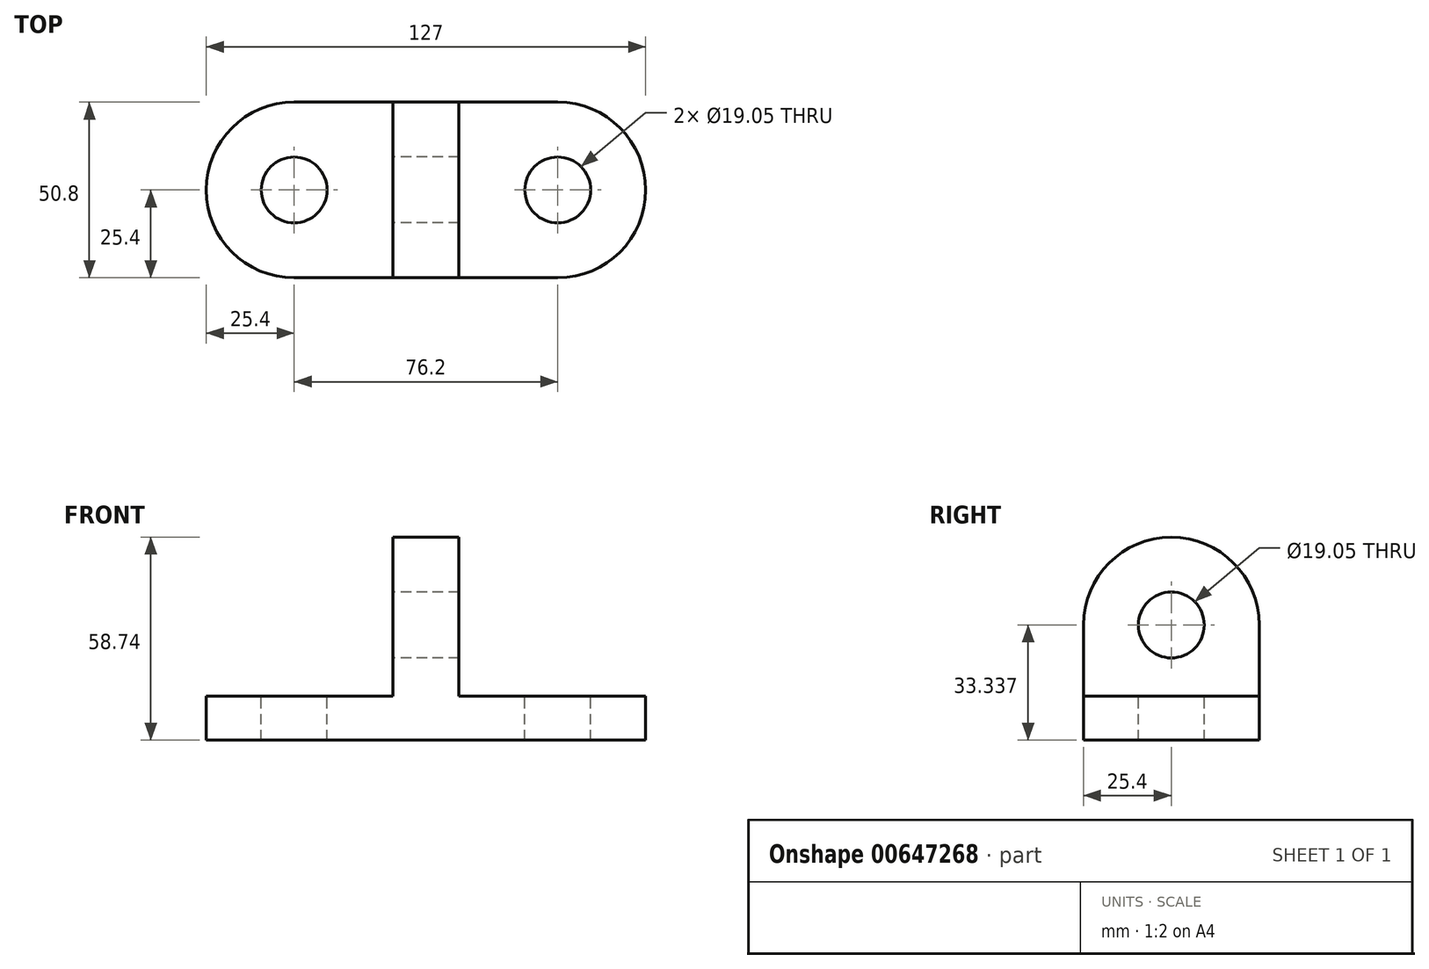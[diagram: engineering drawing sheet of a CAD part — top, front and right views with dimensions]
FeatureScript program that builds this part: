
annotation { "Feature Type Name" : "Feature", "Feature Type Description" : "" }
export const myFeature = defineFeature(function(context is Context, id is Id, definition is map)
    precondition{}
    {
        {
            var Q0;
            Q0=qCreatedBy(makeId("Top.planeOp"),FACE);
            var sketch = newSketch(context, id + "F0", { "sketchPlane" : qUnion([Q0])});
            skLineSegment(sketch, "E0.bottom", {"start": v(-38.1, -25.4) * mm, "end": v(38.1, -25.4) * mm});
            skLineSegment(sketch, "E0.top", {"start": v(-38.1, 25.4) * mm, "end": v(38.1, 25.4) * mm});
            skPoint(sketch, "E0.middle", {"position": v(0, 0) * mm});
            skArc(sketch, "E1", {"start": v(-38.1, -25.4) * mm, "mid": v(-63.5, 0) * mm, "end": v(-38.1, 25.4) * mm});
            skArc(sketch, "E2", {"start": v(38.1, -25.4) * mm, "mid": v(63.5, 0) * mm, "end": v(38.1, 25.4) * mm});
            skSolve(sketch);
        }
        {
            var Q0;
            Q0 = qSketchRegion(id + "F0", true);
            extrude(context, id + "F1", {"entities" : qUnion([Q0]), "depth" : 12.7 * mm, "offsetDistance" : 25.4 * mm});
        }
        {
            var Q0;
            Q0=makeQuery(id+"F1.opExtrude","CAP_FACE",FACE,{"disambiguationData":[OSD([sQuery(id+"F0.wireOp",EDGE,"E0.bottom"),sQuery(id+"F0.wireOp",EDGE,"E0.top"),sQuery(id+"F0.wireOp",EDGE,"E1"),sQuery(id+"F0.wireOp",EDGE,"E2")])],"isStart":false});
            var sketch = newSketch(context, id + "F2", { "sketchPlane" : qUnion([Q0])});
            skCircle(sketch, "E3", {"center": v(-38.1, 0) * mm, "radius": 9.53 * mm});
            skCircle(sketch, "E4", {"center": v(38.1, 0) * mm, "radius": 9.53 * mm});
            skSolve(sketch);
        }
        {
            var Q0;
            Q0=makeQuery(id+"F2.imprint","IMPRINT",FACE,{"disambiguationData":[TD([[makeQuery(id+"F2.imprint","IMPRINT",EDGE,{"derivedFrom":sQuery(id+"F2.wireOp",EDGE,"E3")}),1.0]])]});
            var Q1;
            Q1=makeQuery(id+"F2.imprint","IMPRINT",FACE,{"disambiguationData":[TD([[makeQuery(id+"F2.imprint","IMPRINT",EDGE,{"derivedFrom":sQuery(id+"F2.wireOp",EDGE,"E4")}),1.0]])]});
            extrude(context, id + "F3", {"entities" : qUnion([Q0, Q1]), "operationType" : NewBodyOperationType.REMOVE, "oppositeDirection" : true, "depth" : 12.7 * mm, "offsetDistance" : 25.4 * mm});
        }
        {
            var Q0;
            Q0=qCreatedBy(makeId("Right.planeOp"),FACE);
            var sketch = newSketch(context, id + "F4", { "sketchPlane" : qUnion([Q0])});
            skLineSegment(sketch, "E5", {"start": v(-25.4, 12.7) * mm, "end": v(-25.4, 33.34) * mm});
            skLineSegment(sketch, "E6", {"start": v(25.4, 12.7) * mm, "end": v(25.4, 33.34) * mm});
            skArc(sketch, "E7", {"start": v(-25.4, 33.34) * mm, "mid": v(0, 58.74) * mm, "end": v(25.4, 33.34) * mm});
            skLineSegment(sketch, "E8", {"start": v(25.4, 12.7) * mm, "end": v(-25.4, 12.7) * mm});
            skCircle(sketch, "E9", {"center": v(0, 33.34) * mm, "radius": 9.53 * mm});
            skSolve(sketch);
        }
        {
            var Q0;
            Q0=makeQuery(id+"F4.imprint","IMPRINT",FACE,{"disambiguationData":[TD([[makeQuery(id+"F4.imprint","IMPRINT",EDGE,{"derivedFrom":sQuery(id+"F4.wireOp",EDGE,"E5")}),-1.0]])]});
            extrude(context, id + "F5", {"entities" : qUnion([Q0]), "operationType" : NewBodyOperationType.ADD, "endBound" : BoundingType.SYMMETRIC, "depth" : 19.05 * mm, "offsetDistance" : 25.4 * mm});
        }
    });
